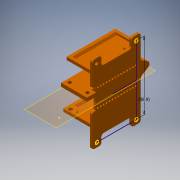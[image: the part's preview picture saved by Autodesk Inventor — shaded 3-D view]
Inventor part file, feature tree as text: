
AUTODESK INVENTOR PART (.ipt)
format: ipt  version: 2017 (Build 210142000, 142)  size: 484,864 bytes
history: native  units: mm
features: extrude x13, sketch x13, other x8, reference x7, projected_geometry x5, chamfer x3, fillet x1
ambient origin geometry x8: Origin, YZ Plane, XZ Plane, XY Plane, X Axis, Y Axis, Z Axis, Center Point
bodies: Solid1 (feature_tree)
feature tree (50):
  extrude  "Extrusion1"  Depth=54.0mm
  extrude  "Extrusion2"  Depth=3.5mm
  extrude  "Extrusion3"  Depth=3.5mm
  chamfer  "Chamfer1"  Distance=150.0mm
  chamfer  "Chamfer2"  Distance=10.0mm
  extrude  "Extrusion4"  Depth=17.9mm
  extrude  "Extrusion5"  Depth=5.0mm
  extrude  "Extrusion6"  Depth=2.0mm TaperAngle=45.0deg
  extrude  "Extrusion7"  Depth=2.0mm
  extrude  "Extrusion8"  Depth=20.0mm
  extrude  "Extrusion9"  Depth=20.0mm
  extrude  "Extrusion10"  Depth=23.0mm
  extrude  "Extrusion11"  Depth=9.25mm
  extrude  "Extrusion12"  Depth=58.9mm
  extrude  "Extrusion13"  Depth=58.9mm
  chamfer  "Chamfer3"  Distance=3.3mm
  fillet  "Fillet1"  Radius=3.3mm
  other  "measure and reference"
  other  "midplane"
  sketch  "Sketch1"  dims[d0=3.0mm d1=0.0mm d3=54.0mm]
  reference  "Reference1"
  reference  "Reference2"
  reference  "Reference3"
  sketch  "Sketch2"  dims[d4=3.5mm d5=4.0mm]
  reference  "Reference4"
  reference  "Reference5"
  reference  "Reference6"
  sketch  "Sketch3"  dims[d6=3.5mm d7=1.75mm]
  sketch  "Sketch4"  dims[d8=2.54mm d9=150.0mm d11=2.54mm d12=10.0mm d14=10.0mm]
  projected_geometry  "Projected Loop1"
  reference  "Reference7"
  sketch  "Sketch5"  dims[d16=17.9mm d17=43.7mm]
  sketch  "Sketch6"  dims[d18=2.0mm d19=0.0mm d20=5.0mm]
  sketch  "Sketch7"  dims[d21=2.0mm d22=0.0mm d23=2.0mm d24=2.0mm d25=45.0deg]
  sketch  "Sketch8"  dims[d26=2.0mm d27=2.0mm d28=45.0deg d29=2.0mm]
  sketch  "Sketch9"  dims[d30=2.0mm d31=0.0mm d32=20.0mm]
  sketch  "Sketch10"  dims[d33=13.0mm d34=20.0mm]
  projected_geometry  "Projected Loop2"
  projected_geometry  "Projected Loop3"
  sketch  "Sketch11"  dims[d35=2.5mm d36=23.0mm]
  sketch  "Sketch12"  dims[d37=2.5mm d38=9.25mm]
  projected_geometry  "Projected Loop4"
  sketch  "Sketch13"  dims[d39=42.0mm d40=0.0mm d41=16.0mm d42=30.4mm d43=3.3mm d44=3.3mm d45=3.0mm d46=0.0mm d47=9.0mm d48=3.75mm d49=10.0mm d50=5.0mm d51=2.0mm d52=0.0mm d53=12.0mm d55=2.0mm d56=0.0mm d57=2.0mm d58=8.0mm d59=8.0mm d60=0.0mm d61=8.0mm d62=0.0mm d63=3.0mm d64=8.0mm d65=0.0mm d66=2.5mm d67=1.5mm d68=0.0mm d69=2.5mm d70=3.0mm d71=3.0mm d72=1.5mm d73=0.0mm d74=1.5mm d75=2.0mm d76=45.0deg d77=58.9mm]
  projected_geometry  "Projected Loop5"
  parser-record x1  (decoder bookkeeping rows leaked as tree rows — omitted from the tree; the rows remain in map.json)
  other  "Ganymede Node.iam"
  other  "moist probe:1"
  other  "soil sensor:1"
  other  "NanoV3 v4:1"
  other  "NRF24L01+:1"
note: 1 file-system path scrubbed to <path> (originals preserved in map.json)
